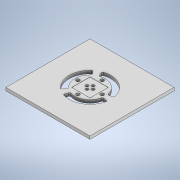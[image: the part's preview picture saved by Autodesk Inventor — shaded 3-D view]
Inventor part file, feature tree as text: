
AUTODESK INVENTOR PART (.ipt)
format: ipt  version: 2022 (Build 260153000, 153)  size: 414,720 bytes
history: native  units: in
note: dims shown in document units (in); Inventor stores cm internally (conversion verified against a paired STEP export)
features: thicken_offset x10, extrude x6, sketch x6, projected_geometry x5, other x3, reference x2, chamfer x1, fillet x1
ambient origin geometry x8: Origin, YZ Plane, XZ Plane, XY Plane, X Axis, Y Axis, Z Axis, Center Point
bodies: Solid1 (feature_tree)
feature tree (34):
  extrude  "Extrusion1"  Depth=2.2638in
  extrude  "Extrusion2"  Depth=0.1in
  chamfer  "Chamfer1"  Distance=0.05in
  extrude  "Extrusion3"  Depth=0.1in
  extrude  "Extrusion4"  Depth=0.1in
  fillet  "Fillet1"  Radius=1.0046in
  extrude  "Extrusion5"  Depth=0.05in TaperAngle=0.0deg
  thicken_offset  "Thicken1"
  extrude  "Extrusion6"  Depth=0.05in TaperAngle=45.0deg
  thicken_offset  "Thicken2"
  thicken_offset  "Thicken3"
  thicken_offset  "Thicken4"
  thicken_offset  "Thicken5"
  thicken_offset  "Thicken6"
  thicken_offset  "Thicken7"
  thicken_offset  "Thicken8"
  thicken_offset  "Thicken9"
  thicken_offset  "Thicken10"
  sketch  "Sketch1"  dims[d0=2.2638in d1=2.2638in]
  sketch  "Sketch2"  dims[d2=0.1in d3=0.0in d4=0.7546in d5=0.7546in]
  projected_geometry  "Projected Loop1"
  sketch  "Sketch3"  dims[d6=0.7546in]
  projected_geometry  "Projected Loop2"
  sketch  "Sketch4"  dims[d7=0.7546in]
  projected_geometry  "Projected Loop3"
  sketch  "Sketch5"  dims[d8=0.7546in]
  reference  "Reference1"
  reference  "Reference2"
  sketch  "Sketch6"  dims[d9=0.05in d10=0.05in d11=0.55in d12=0.55in d13=1.1811in d15=1.0046in d16=1.1811in d18=1.0046in d21=0.05in d22=0.0in d23=0.05in d24=0.125in d25=45.0deg d26=0.3in d27=0.3in d28=0.005in d29=0.0in d30=0.6in d31=0.6in d32=1.0in d33=0.0in d34=0.0in d35=120.0deg d36=120.0deg d37=0.0in d38=0.7559in d39=0.8933in d40=0.7559in d41=0.8933in d42=0.0687in d43=0.0687in d44=0.035in d45=0.05in d46=0.0in d47=1.5546in d48=1.355in d49=0.25in d50=0.25in d51=0.374in d52=0.374in d53=0.1in d54=0.1in d55=0.0in d56=0.1in d57=90.0deg d58=0.05in d59=0.05in d60=0.05in d61=1.0in d62=0.0in d63=0.1in d64=0.1in d65=0.1in d66=0.1in d67=0.1in d68=0.1in d69=0.1in d70=0.1181in d71=0.1181in d72=0.01in d73=0.01in d74=0.01in d75=0.01in d76=0.01in d77=0.01in d78=0.01in d79=0.01in d80=0.01in d81=0.01in d82=0.01in d83=0.01in d84=0.01in d85=0.01in d86=0.01in d87=0.01in d88=0.01in d89=0.01in]
  projected_geometry  "Projected Loop4"
  projected_geometry  "Projected Loop5"
  parser-record x1  (decoder bookkeeping rows leaked as tree rows — omitted from the tree; the rows remain in map.json)
  other  "CubeAssembly.iam"
  other  "SpringPotBottom:2"
note: 1 file-system path scrubbed to <path> (originals preserved in map.json)
